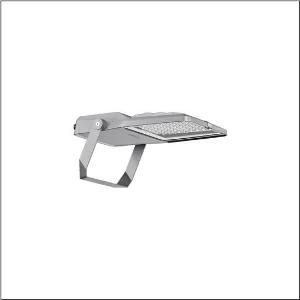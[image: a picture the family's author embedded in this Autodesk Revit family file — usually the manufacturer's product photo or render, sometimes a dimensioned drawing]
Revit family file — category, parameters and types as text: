
# Revit family: floodlight_fl_21_iq_mini___pl43_5xa7772c3a1a_2542
name_source: partatom
category: Lighting Fixtures
units: mm (PartAtom-declared; Revit-internal decimal feet)

## family parameters
Cut with Voids When Loaded = No
Host = Face
Light Source = No
Part Type = Normal
Room Calculation Point = No
Round Connector Dimension = Use Diameter
Shared = No

## types (1)
- --- (1 x LED, 10780 lm, 87.2 W, 3000K)
    Apparent Load = 87 VA
    CIE Flux Codes = 27 78 99 100 100
    Color Rendering = 80
    Color Temperature = 3000K
    Default Elevation = 1800 mm
    Description = Floodlight FL 21 iQ mini, floodlight, primary light control with lens, of PMMA, primary optical cover: protective disc, of toughened safety glass, transparent, light distribution: PL43, light emission: direct distribution, installation type: surface-mounted, LED, High Power LED, rated luminous flux: 10.780lm, luminous efficacy: 124lm/W, light colour: 830, colour temperature: 3000K, control: Street-Remote, Auto-Match, Temp-Guard, Night-Set, Smart-Wire, Desk-Remote (wireless, voltage-free reading and setting of iQ features in the workshop via application-optimized NFC function/RFID function), optimised constant luminous flux control (CLO 2.0), with terminal, 6-pole, mains connection: 220..240V, AC, 50/60Hz, start of lifetime: 87W, end of service life: 92W, reduction: 40W, luminaire housing, of diecast aluminium, powder-coated, Siteco® metallic grey (DB 702S), corrosivity category C5 mid according to DIN EN ISO 12944, sealing non-destructively replaceable, mounting bracket, of steel, galvanised, powder-coated, Siteco® metallic grey (DB 702S), protection rating (complete): IP66, insulation class (complete): insulation class II (safety insulation), certification: CE, ENEC, VDE, protection symbol: D, impact resistance: IK08, permissible operating ambient temperature: -40..+40°C, permissible operating ambient temperature for outdoor applications: -40..+50°C, standard: DIN EN 12944, LABS conformity tested according to VDMA 24364:2018-05, packaging unit: 1 piece

Light Distribution: PL43
    Height = 70 mm
    Lamp = 1 x LED
    Lamp Light Flux = 10780 lm
    Lamp Power = 87.2 W
    Lamp count = 1
    Length = 485 mm
    Luminous efficacy = 124 lm/W
    Manufacturer = Siteco
    ModVariant = No
    Model = 5XA7772C3A1A
    Number of Poles = 1
    OnlyDefault = Yes
    Power Factor = 1
    Product Name = Floodlight FL 21 iQ mini | PL43
    Product group = floodlight | pylon annexe
    ProductGroupID = 6200
    Protection Class = Protection class II
    Protection Degree = IP 66
    RLX_Detail_Level = 1
    RLX_Emergency_Light_Flux = 0 lm
    RLX_Emergency_Type = 0
    RLX_Emergency_Type_DB = No
    RlxData = <blob elided: 96157 chars, md5=0afefc5e>
    Socket = socket
    Standby Power = 0 W
    System Light Flux = 10780 lm
    System Power = 87 W
    Type Comments = factory setting: luminous flux: 100 % | dim-lin: 254 | 456 mA
    Type Image = l_1006845.jpg
    URL = http://relux.com
    VarID = @adj_094569
    Voltage = 0 V
    Weight = 0.00 kg
    Width = 337 mm

## geometry (parser evidence)
native form markers: Blend x4, Sweep x10
no freeform markers — native parametric forms only
